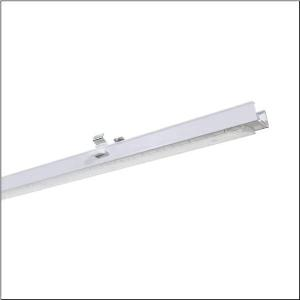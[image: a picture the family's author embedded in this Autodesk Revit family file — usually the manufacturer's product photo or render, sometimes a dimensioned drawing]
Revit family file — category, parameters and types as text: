
# Revit family: trunking_flex_31_51re12mb48b
name_source: partatom
category: Lighting Fixtures
units: mm (PartAtom-declared; Revit-internal decimal feet)

## family parameters
Cut with Voids When Loaded = No
Host = Face
Light Source = No
Part Type = Normal
Room Calculation Point = No
Round Connector Dimension = Use Diameter
Shared = No

## types (1)
- --- (1 x LED, 8000 lm, 50 W, 4000K)
    Apparent Load = 50 VA
    CIE Flux Codes = 65 91 98 99 100
    Color Rendering = 80
    Color Temperature = 4000K
    Default Elevation = 1800 mm
    Description = Trunking Flex 31, luminaire insert, of extruded aluminium section, coated, traffic white (RAL 9016), length: 1.472mm, width: 91mm, height: 53mm, LED rated luminous flux: 8.000lm, light colour: 840, control gear: ON/OFF Multilumen, with system connector: socket, mains connection: 220..240V, AC, 50/60Hz, rated input power: 50W, luminous flux adjustable on luminaire in four steps (4130/5610/6850/8000lm), connected load according to luminous flux setting (25/34/42/50W), primary light control with lens, of plastic, primary optical cover: cover, of PMMA, light emission: direct distribution, protection rating (complete): IP20, insulation class (complete): insulation class I (protective earthing), certification: CE, UKCA, impact resistance: IK02, permissible ambient temperature for indoor applications: -20..+40°C, packaging unit: 1 piece
    Height = 58 mm
    Lamp = 1 x LED
    Lamp Light Flux = 8000 lm
    Lamp Power = 50 W
    Lamp count = 1
    Length = 1472 mm
    Luminous efficacy = 160 lm/W
    Manufacturer = Siteco
    ModVariant = No
    Model = 51RE12MB48B
    Mounting Place = Ceiling
    Mounting Type = Pendant
    Number of Poles = 1
    OnlyDefault = Yes
    Power Factor = 1
    Product Name = Trunking Flex 31
    Product group = luminaire insert
    ProductGroupID = 901
    Protection Class = Protection class I
    Protection Degree = IP 20
    RLX_Detail_Level = 1
    RLX_Emergency_Light_Flux = 0 lm
    RLX_Emergency_Type = 0
    RLX_Emergency_Type_DB = No
    RlxData = <blob elided: 20341 chars, md5=45fa833a>
    Socket = socket
    Standby Power = 0 W
    System Light Flux = 8000 lm
    System Power = 50 W
    Type Comments = factory setting: luminous flux: 100 % | (ON | ON) | 300 mA
    Type Image = l_1266702.jpg
    URL = http://relux.com
    VarID = @adj_018657
    Voltage = 0 V
    Weight = 0.00 kg
    Width = 65 mm

## geometry (parser evidence)
native form markers: Blend x4, Sweep x9
no freeform markers — native parametric forms only
